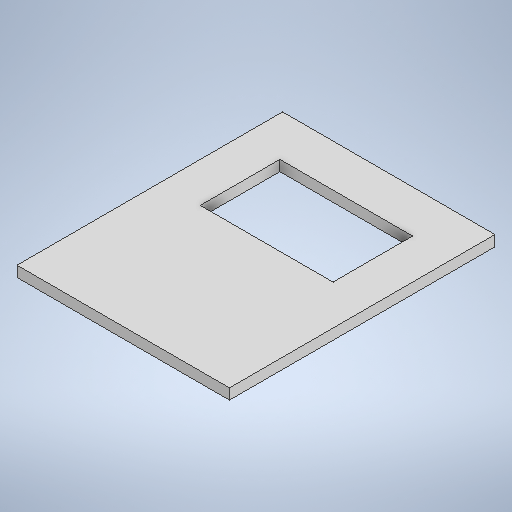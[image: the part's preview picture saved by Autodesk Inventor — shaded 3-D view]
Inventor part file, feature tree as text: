
AUTODESK INVENTOR PART (.ipt)
format: ipt  version: 2025.1 (Build 291241000, 241)  size: 244,736 bytes
history: native  units: mm
features: extrude x2, sketch x2
ambient origin geometry x8: Origin, YZ Plane, XZ Plane, XY Plane, X Axis, Y Axis, Z Axis, Center Point
bodies: Volumenkörper1 (feature_tree)
feature tree (4):
  extrude  "Extrusion1"  Depth=500.0mm
  extrude  "Extrusion2"  Depth=150.0mm
  sketch  "Skizze1"  dims[d0=400.0mm d1=500.0mm]
  sketch  "Skizze2"  dims[d2=20.0mm d3=0.0mm d4=150.0mm d5=250.0mm d6=80.0mm d7=20.0mm d8=0.0mm]
